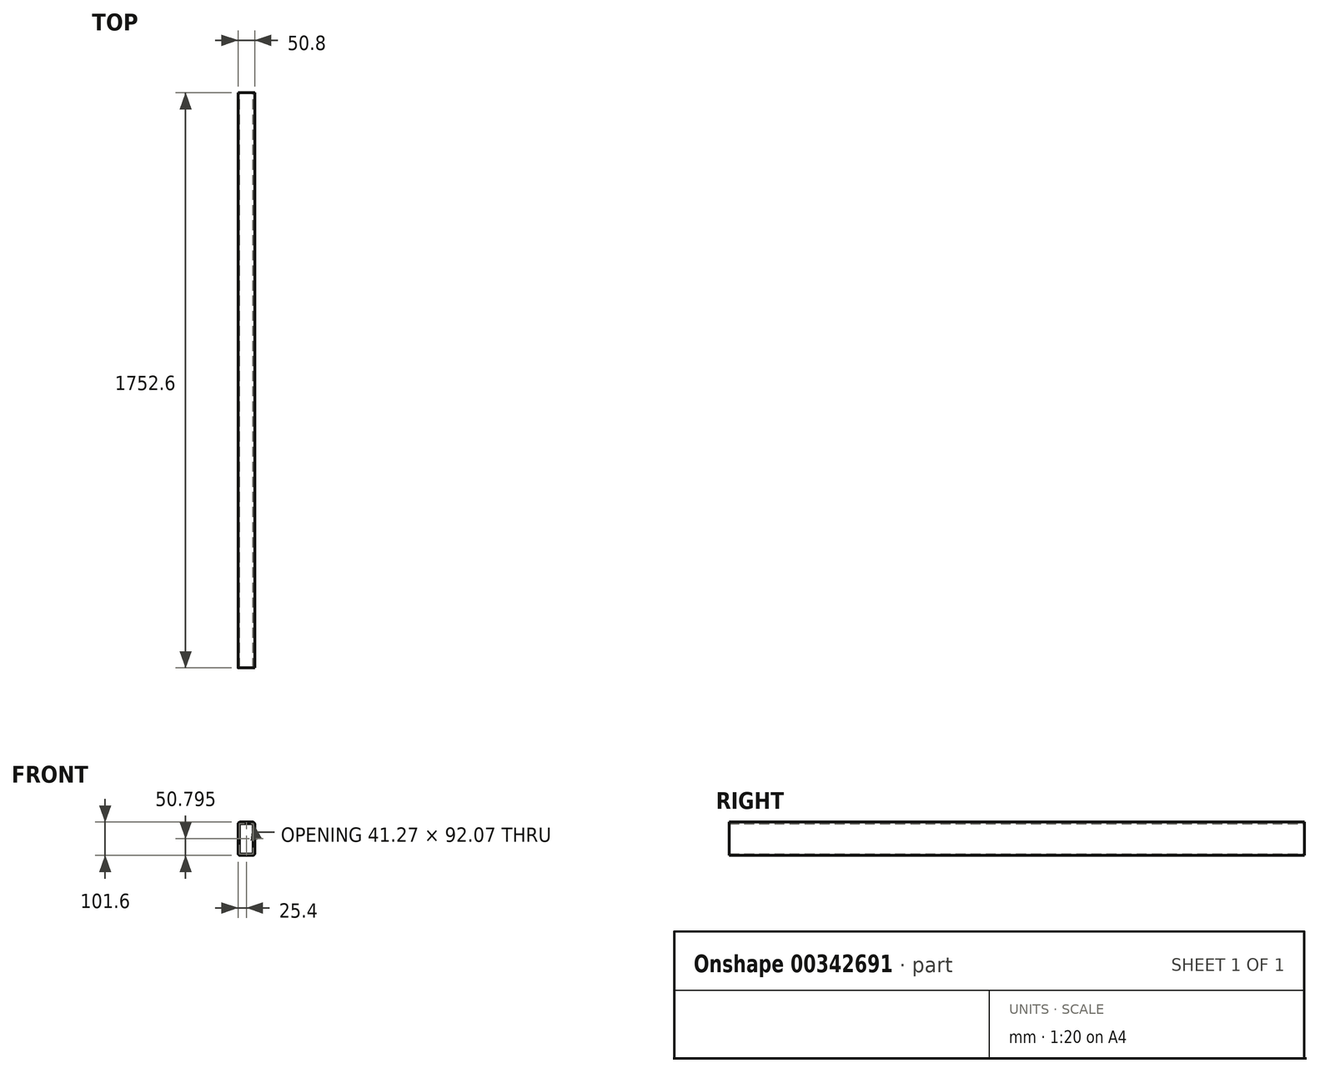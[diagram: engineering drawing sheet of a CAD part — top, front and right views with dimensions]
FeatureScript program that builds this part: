
annotation { "Feature Type Name" : "Feature", "Feature Type Description" : "" }
export const myFeature = defineFeature(function(context is Context, id is Id, definition is map)
    precondition{}
    {
        {
            var Q0;
            Q0=qCreatedBy(makeId("Front.planeOp"),FACE);
            var sketch = newSketch(context, id + "F0", { "sketchPlane" : qUnion([Q0])});
            skLineSegment(sketch, "E0.bottom", {"start": v(-19.05, 50.8) * mm, "end": v(19.05, 50.8) * mm});
            skLineSegment(sketch, "E0.top", {"start": v(-19.05, -50.8) * mm, "end": v(19.05, -50.8) * mm});
            skLineSegment(sketch, "E0.left", {"start": v(-25.4, 44.45) * mm, "end": v(-25.4, -44.45) * mm});
            skLineSegment(sketch, "E0.right", {"start": v(25.4, 44.45) * mm, "end": v(25.4, -44.45) * mm});
            skPoint(sketch, "E0.middle", {"position": v(0, 0) * mm});
            skPoint(sketch, "E1.visualSharp", {"position": v(-25.4, 50.8) * mm});
            skArc(sketch, "E1.filletArc", {"start": v(-19.05, 50.8) * mm, "mid": v(-23.54, 48.94) * mm, "end": v(-25.4, 44.45) * mm});
            skPoint(sketch, "E2.visualSharp", {"position": v(25.4, 50.8) * mm});
            skArc(sketch, "E2.filletArc", {"start": v(25.4, 44.45) * mm, "mid": v(23.54, 48.94) * mm, "end": v(19.05, 50.8) * mm});
            skPoint(sketch, "E3.visualSharp", {"position": v(25.4, -50.8) * mm});
            skArc(sketch, "E3.filletArc", {"start": v(19.05, -50.8) * mm, "mid": v(23.54, -48.94) * mm, "end": v(25.4, -44.45) * mm});
            skPoint(sketch, "E4.visualSharp", {"position": v(-25.4, -50.8) * mm});
            skArc(sketch, "E4.filletArc", {"start": v(-25.4, -44.45) * mm, "mid": v(-23.54, -48.94) * mm, "end": v(-19.05, -50.8) * mm});
            skLineSegment(sketch, "E5.0", {"start": v(-19.05, 46.03) * mm, "end": v(19.05, 46.03) * mm});
            skLineSegment(sketch, "E5.1", {"start": v(-20.64, 44.44) * mm, "end": v(-20.64, -44.45) * mm});
            skLineSegment(sketch, "E5.2", {"start": v(-19.05, -46.04) * mm, "end": v(19.05, -46.04) * mm});
            skLineSegment(sketch, "E5.3", {"start": v(20.64, 44.44) * mm, "end": v(20.64, -44.45) * mm});
            skPoint(sketch, "E6.visualSharp", {"position": v(-20.64, 46.03) * mm});
            skArc(sketch, "E6.filletArc", {"start": v(-19.05, 46.03) * mm, "mid": v(-20.17, 45.56) * mm, "end": v(-20.64, 44.44) * mm});
            skPoint(sketch, "E7.visualSharp", {"position": v(20.64, 46.03) * mm});
            skArc(sketch, "E7.filletArc", {"start": v(20.64, 44.44) * mm, "mid": v(20.17, 45.56) * mm, "end": v(19.05, 46.03) * mm});
            skPoint(sketch, "E8.visualSharp", {"position": v(20.64, -46.04) * mm});
            skArc(sketch, "E8.filletArc", {"start": v(19.05, -46.04) * mm, "mid": v(20.17, -45.57) * mm, "end": v(20.64, -44.45) * mm});
            skPoint(sketch, "E9.visualSharp", {"position": v(-20.64, -46.04) * mm});
            skArc(sketch, "E9.filletArc", {"start": v(-20.64, -44.45) * mm, "mid": v(-20.17, -45.57) * mm, "end": v(-19.05, -46.04) * mm});
            skSolve(sketch);
        }
        {
            var Q0;
            Q0=makeQuery(id+"F0.imprint","IMPRINT",FACE,{"disambiguationData":[TD([[makeQuery(id+"F0.imprint","IMPRINT",EDGE,{"derivedFrom":sQuery(id+"F0.wireOp",EDGE,"E0.bottom")}),-1.0]])]});
            extrude(context, id + "F1", {"entities" : qUnion([Q0]), "depth" : 1752.6 * mm});
        }
    });
